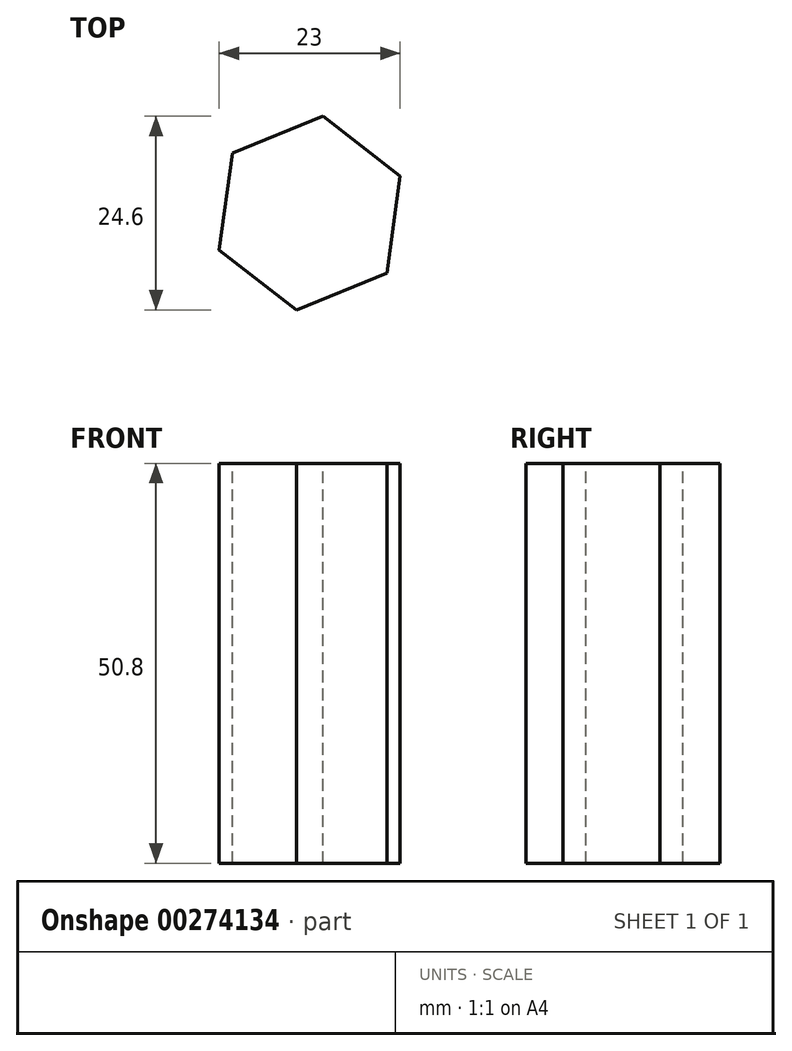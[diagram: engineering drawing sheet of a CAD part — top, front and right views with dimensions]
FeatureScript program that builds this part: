
annotation { "Feature Type Name" : "Feature", "Feature Type Description" : "" }
export const myFeature = defineFeature(function(context is Context, id is Id, definition is map)
    precondition{}
    {
        {
            var Q0;
            Q0=qCreatedBy(makeId("Top.planeOp"),FACE);
            var sketch = newSketch(context, id + "F0", { "sketchPlane" : qUnion([Q0])});
            skCircle(sketch, "E0.cCircle", {"center": v(0, 0) * mm, "radius": 10.75 * mm, "construction": true});
            skLineSegment(sketch, "E0.0", {"start": v(-9.8, 7.61) * mm, "end": v(1.7, 12.3) * mm});
            skLineSegment(sketch, "E0.1", {"start": v(1.7, 12.3) * mm, "end": v(11.5, 4.68) * mm});
            skLineSegment(sketch, "E0.2", {"start": v(11.5, 4.68) * mm, "end": v(9.8, -7.61) * mm});
            skLineSegment(sketch, "E0.3", {"start": v(9.8, -7.61) * mm, "end": v(-1.7, -12.3) * mm});
            skLineSegment(sketch, "E0.4", {"start": v(-1.7, -12.3) * mm, "end": v(-11.5, -4.68) * mm});
            skLineSegment(sketch, "E0.5", {"start": v(-11.5, -4.68) * mm, "end": v(-9.8, 7.61) * mm});
            skPoint(sketch, "E0.0.midPoint", {"position": v(-4.06, 9.96) * mm});
            skSolve(sketch);
        }
        {
            var Q0;
            Q0=qCreatedBy(makeId("Front.planeOp"),FACE);
            var sketch = newSketch(context, id + "F1", { "sketchPlane" : qUnion([Q0])});
            skLineSegment(sketch, "E1", {"start": v(0, -3.17) * mm, "end": v(0, 47.63) * mm});
            skSolve(sketch);
        }
        {
            var Q0;
            Q0=makeQuery(id+"F0.imprint","IMPRINT",FACE,{"disambiguationData":[TD([[makeQuery(id+"F0.imprint","IMPRINT",EDGE,{"derivedFrom":sQuery(id+"F0.wireOp",EDGE,"E0.0")}),-1.0]])]});
            var Q1;
            Q1=sQuery(id+"F1.wireOp",EDGE,"E1");
            sweep(context, id + "F2", {"profiles" : qUnion([Q0]), "path" : qUnion([Q1])});
        }
    });
